# Revit family: Adult_Changing_Station-Adjustable_Height-Koala_Kare-KB2600_Open_Series
name_source: partatom
category: Specialty Equipment
units: mm (PartAtom-declared; Revit-internal decimal feet)

## family parameters
Cut with Voids When Loaded = No
Host = Face
OmniClass Number = 23.40.20.21
OmniClass Title = Toilet and Bath Specialties
Part Type = Normal
Room Calculation Point = No
Round Connector Dimension = Use Diameter
Shared = Yes

## types (2) — shared parameters
Assembly Code = E2010
Default Elevation = 0"
Description = Adjustable Height Changing Station
Electrical Description = 110v, electrical outlet
Frame and Guard Material = Stainless Steel-Koala Kare-Powder Coated White
Height = 60 13/32"
Installation Type = Wall Mounted
Length = 70 7/8"
Load Capacity = 220lbs
Manufacturer = Koala Kare
Model = KB2600
Stretcher Material = Vinyl-Koala Kare-White
URL = https://www.koalabear.com
Wall Cover Material = ABS-Koala Kare-Acrylic
Width = 45 11/16"

## per-type parameters (varying)
| type | Stretcher Extension Open | Stretcher Extension Vertical |
| KB3000-Stretcher Extension Open | Yes | No |
| KB3000-Stretcher Extension Vertical | No | Yes |

note: column(s) folded — value = type name in every type: Type Comments

## geometry (parser evidence)
native form markers: Sweep x2
no freeform markers — native parametric forms only
